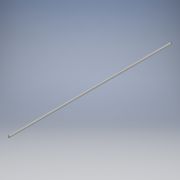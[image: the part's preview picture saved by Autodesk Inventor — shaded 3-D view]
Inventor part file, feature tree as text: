
AUTODESK INVENTOR PART (.ipt)
format: ipt  version: 2016 (Build 200138000, 138)  size: 86,528 bytes
history: native  units: in
note: dims shown in document units (in); Inventor stores cm internally (conversion verified against a paired STEP export)
features: extrude x1, sketch x1
ambient origin geometry x8: Origin, YZ Plane, XZ Plane, XY Plane, X Axis, Y Axis, Z Axis, Center Point
bodies: Solid1 (feature_tree)
feature tree (2):
  extrude  "Extrusion1"  Depth=12.0in TaperAngle=0.0deg
  sketch  "Sketch1"  dims[d0=0.125in d1=12.0in d2=0.0in]
